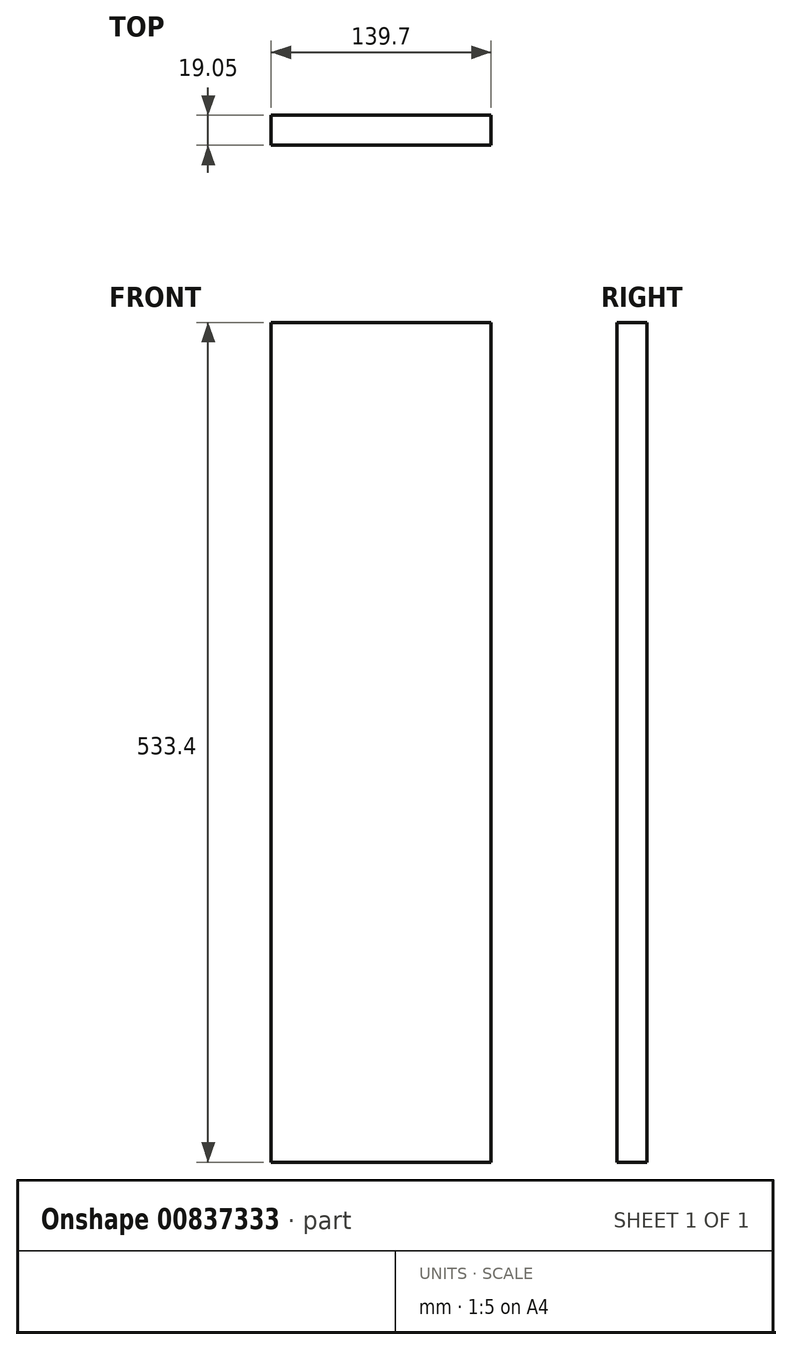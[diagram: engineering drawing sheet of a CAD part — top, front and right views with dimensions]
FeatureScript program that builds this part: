
annotation { "Feature Type Name" : "Feature", "Feature Type Description" : "" }
export const myFeature = defineFeature(function(context is Context, id is Id, definition is map)
    precondition{}
    {
        {
            var Q0;
            Q0=qCreatedBy(makeId("Front.planeOp"),FACE);
            var sketch = newSketch(context, id + "F0", { "sketchPlane" : qUnion([Q0])});
            skLineSegment(sketch, "E0.bottom", {"start": v(0, 0) * mm, "end": v(139.7, 0) * mm});
            skLineSegment(sketch, "E0.top", {"start": v(0, 533.4) * mm, "end": v(139.7, 533.4) * mm});
            skLineSegment(sketch, "E0.left", {"start": v(0, 0) * mm, "end": v(0, 533.4) * mm});
            skLineSegment(sketch, "E0.right", {"start": v(139.7, 0) * mm, "end": v(139.7, 533.4) * mm});
            skSolve(sketch);
        }
        {
            var Q0;
            Q0=makeQuery(id+"F0.imprint","IMPRINT",FACE,{"disambiguationData":[TD([[makeQuery(id+"F0.imprint","IMPRINT",EDGE,{"derivedFrom":sQuery(id+"F0.wireOp",EDGE,"E0.bottom")}),1.0]])]});
            extrude(context, id + "F1", {"entities" : qUnion([Q0]), "depth" : 19.05 * mm, "offsetDistance" : 25.4 * mm});
        }
    });
